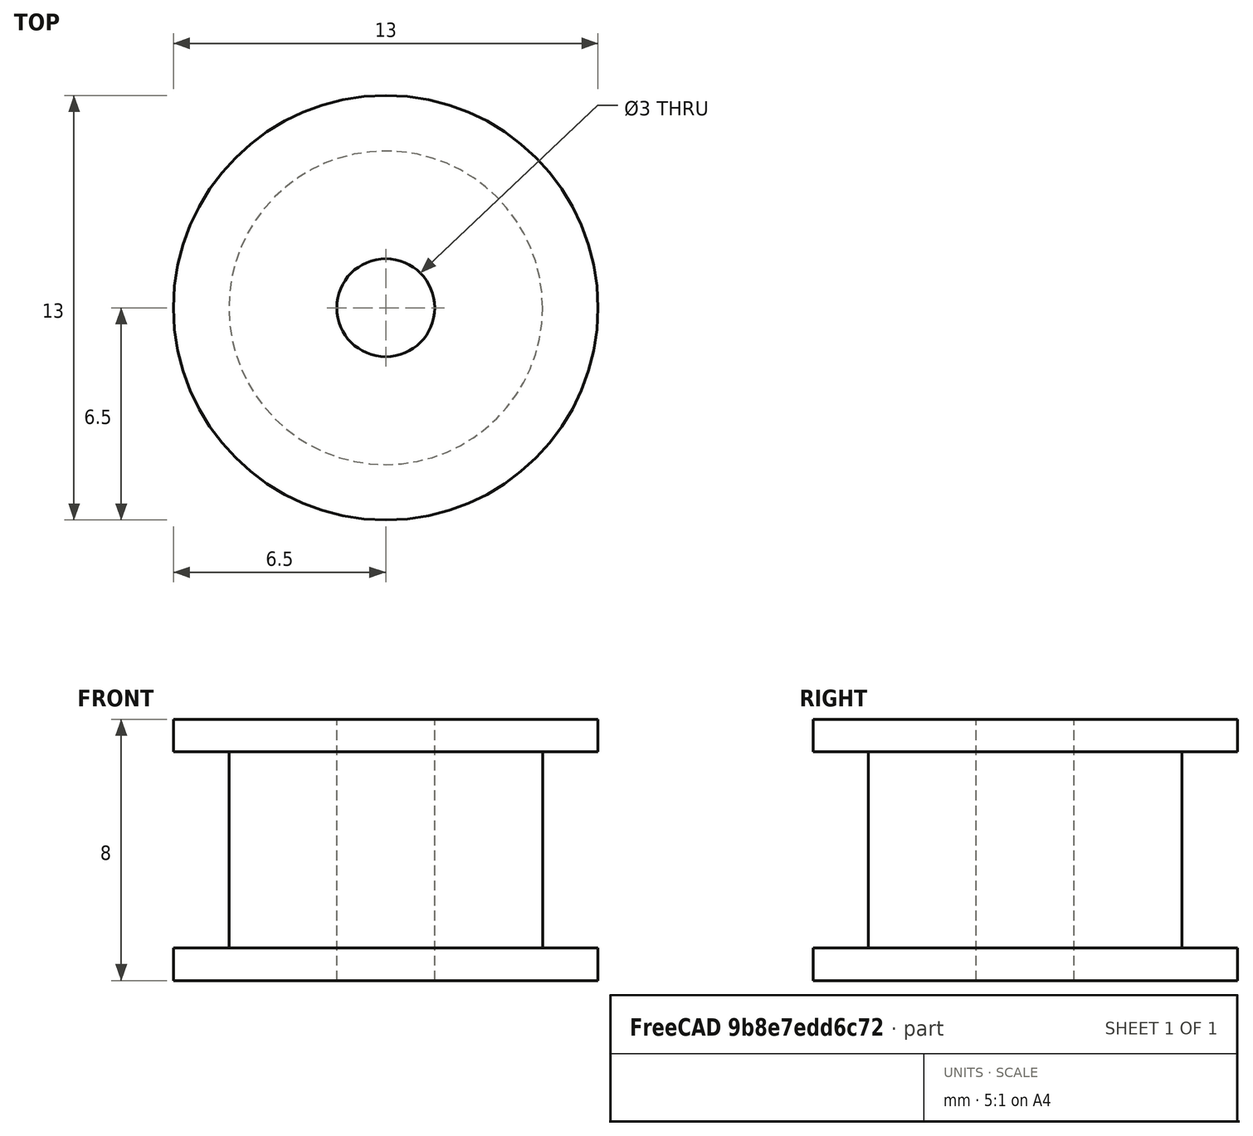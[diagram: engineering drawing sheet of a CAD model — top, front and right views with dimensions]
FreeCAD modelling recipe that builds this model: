
FCSTD DOCUMENT  (FreeCAD 0.18R14555 (Git shallow))
Label: idler-pulley
License: All rights reserved
LicenseURL: http://en.wikipedia.org/wiki/All_rights_reserved
objects: Sketcher::SketchObject×1, PartDesign::Revolution×1, PartDesign::Body×1
note: 4 computed .brp shape members not serialized (recipe doc carries the construction recipe); baked Part::Feature solids carry a one-line shape summary decoded from their .brp

FEATURE [Sketcher::SketchObject] Sketch
  MapMode = 5
  Placement = pos=(0,0,0) rot=(1,0,0;1.5708rad)
  Support = -> [XZ_Plane]
  sketch-geometry (11):
    g0: LineSegment StartX=1.5 StartY=-4 StartZ=0 EndX=1.5 EndY=4 EndZ=0
    g1: LineSegment StartX=1.5 StartY=4 StartZ=0 EndX=6.5 EndY=4 EndZ=0
    g2: LineSegment StartX=6.5 StartY=4 StartZ=0 EndX=6.5 EndY=3 EndZ=0
    g3: LineSegment StartX=6.5 StartY=3 StartZ=0 EndX=4.8 EndY=3 EndZ=0
    g4: LineSegment StartX=4.8 StartY=3 StartZ=0 EndX=4.8 EndY=-3 EndZ=0
    g5: LineSegment StartX=4.8 StartY=-3 StartZ=0 EndX=6.5 EndY=-3 EndZ=0
    g6: LineSegment StartX=6.5 StartY=-3 StartZ=0 EndX=6.5 EndY=-4 EndZ=0
    g7: LineSegment StartX=6.5 StartY=-4 StartZ=0 EndX=1.5 EndY=-4 EndZ=0
    g8: LineSegment [constr] StartX=6.5 StartY=-3 StartZ=0 EndX=6.5 EndY=3 EndZ=0
    g9: LineSegment [constr] StartX=1.5 StartY=-4 StartZ=0 EndX=0 EndY=-4e-16 EndZ=0
    g10: LineSegment [constr] StartX=0 StartY=0 StartZ=0 EndX=1.5 EndY=4 EndZ=0
  constraints (30):
    c: Vertical(g0)
    c: Coincident(g0,g1)
    c: Horizontal(g1)
    c: Coincident(g1,g2)
    c: Vertical(g2)
    c: Coincident(g2,g3)
    c: Horizontal(g3)
    c: Coincident(g3,g4)
    c: Vertical(g4)
    c: Coincident(g4,g5)
    c: Horizontal(g5)
    c: Coincident(g5,g6)
    c: Vertical(g6)
    c: Coincident(g6,g7)
    c: Coincident(g7,g0)
    c: Horizontal(g7)
    c: Coincident(g8,g5)
    c: Coincident(g8,g2)
    c: Vertical(g8)
    c: Coincident(g9,g0)
    c: Coincident(g9,g-1)
    c: Coincident(g10,g-1)
    c: Coincident(g10,g0)
    c: Equal(g10,g9)
    c: Equal(g2,g6)
    c: DistanceX(g-1,g0) = 1.5
    c: DistanceX(g-1,g1) = 6.5
    c: DistanceX(g-1,g3) = 4.8
    c: DistanceY(g5,g2) = 6
    c: DistanceY(g2,g2) = 1
FEATURE [PartDesign::Revolution] Revolution
  Angle = 360
  Axis = (0,2e-16,1)
  Base = (0,0,0)
  Placement = pos=(0,0,0) rot=(1,0,0;1.5708rad)
  Profile = -> Sketch
  ReferenceAxis = -> Sketch [V_Axis]
  Reversed = true
FEATURE [PartDesign::Body] Body
  Group = -> [Sketch,Revolution]
  Origin = -> Origin
  Tip = -> Revolution
